FCSTD DOCUMENT  (FreeCAD 0.16R6707 (Git))
Label: temp
License: All rights reserved
LicenseURL: http://en.wikipedia.org/wiki/All_rights_reserved
objects: Sketcher::SketchObject×1
note: 1 computed .brp shape members not serialized (recipe doc carries the construction recipe); baked Part::Feature solids carry a one-line shape summary decoded from their .brp

FEATURE [Sketcher::SketchObject] Sketch006
  sketch-geometry (47):
    g0: LineSegment [constr] StartX=-190 StartY=250 StartZ=0 EndX=0 EndY=250 EndZ=0
    g1: LineSegment [constr] StartX=0 StartY=250 StartZ=0 EndX=0 EndY=0 EndZ=0
    g2: LineSegment [constr] StartX=0 StartY=0 StartZ=0 EndX=-190 EndY=0 EndZ=0
    g3: LineSegment [constr] StartX=-190 StartY=0 StartZ=0 EndX=-190 EndY=250 EndZ=0
    g4: LineSegment [constr] StartX=-152.5 StartY=78.75 StartZ=0 EndX=-37.5 EndY=78.75 EndZ=0
    g5: LineSegment [constr] StartX=-37.5 StartY=78.75 StartZ=0 EndX=-37.5 EndY=13.75 EndZ=0
    g6: LineSegment [constr] StartX=-37.5 StartY=13.75 StartZ=0 EndX=-152.5 EndY=13.75 EndZ=0
    g7: LineSegment [constr] StartX=-152.5 StartY=13.75 StartZ=0 EndX=-152.5 EndY=78.75 EndZ=0
    g8: Circle CenterX=-147.5 CenterY=68.75 CenterZ=0 NormalX=0 NormalY=0 NormalZ=1 Radius=2
    g9: Circle CenterX=-147.5 CenterY=23.75 CenterZ=0 NormalX=0 NormalY=0 NormalZ=1 Radius=2
    g10: Circle CenterX=-42.5 CenterY=68.75 CenterZ=0 NormalX=0 NormalY=0 NormalZ=1 Radius=2
    g11: Circle CenterX=-42.5 CenterY=23.75 CenterZ=0 NormalX=0 NormalY=0 NormalZ=1 Radius=2
    g12: LineSegment [constr] StartX=-152.5 StartY=78.75 StartZ=0 EndX=-147.5 EndY=68.75 EndZ=0
    g13: LineSegment [constr] StartX=-152.5 StartY=13.75 StartZ=0 EndX=-147.5 EndY=23.75 EndZ=0
    g14: LineSegment [constr] StartX=-42.5 StartY=23.75 StartZ=0 EndX=-37.5 EndY=13.75 EndZ=0
    g15: LineSegment [constr] StartX=-152.5 StartY=157.5 StartZ=0 EndX=-37.5 EndY=157.5 EndZ=0
    g16: LineSegment [constr] StartX=-37.5 StartY=157.5 StartZ=0 EndX=-37.5 EndY=92.5 EndZ=0
    g17: LineSegment [constr] StartX=-37.5 StartY=92.5 StartZ=0 EndX=-152.5 EndY=92.5 EndZ=0
    g18: LineSegment [constr] StartX=-152.5 StartY=92.5 StartZ=0 EndX=-152.5 EndY=157.5 EndZ=0
    g19: Circle CenterX=-147.5 CenterY=147.5 CenterZ=0 NormalX=0 NormalY=0 NormalZ=1 Radius=2
    g20: Circle CenterX=-147.5 CenterY=102.5 CenterZ=0 NormalX=0 NormalY=0 NormalZ=1 Radius=2
    g21: Circle CenterX=-42.5 CenterY=147.5 CenterZ=0 NormalX=0 NormalY=0 NormalZ=1 Radius=2
    g22: Circle CenterX=-42.5 CenterY=102.5 CenterZ=0 NormalX=0 NormalY=0 NormalZ=1 Radius=2
    g23: LineSegment [constr] StartX=-152.5 StartY=157.5 StartZ=0 EndX=-147.5 EndY=147.5 EndZ=0
    g24: LineSegment [constr] StartX=-152.5 StartY=92.5 StartZ=0 EndX=-147.5 EndY=102.5 EndZ=0
    g25: LineSegment [constr] StartX=-42.5 StartY=102.5 StartZ=0 EndX=-37.5 EndY=92.5 EndZ=0
    g26: LineSegment [constr] StartX=-152.5 StartY=236.25 StartZ=0 EndX=-37.5 EndY=236.25 EndZ=0
    g27: LineSegment [constr] StartX=-37.5 StartY=236.25 StartZ=0 EndX=-37.5 EndY=171.25 EndZ=0
    g28: LineSegment [constr] StartX=-37.5 StartY=171.25 StartZ=0 EndX=-152.5 EndY=171.25 EndZ=0
    g29: LineSegment [constr] StartX=-152.5 StartY=171.25 StartZ=0 EndX=-152.5 EndY=236.25 EndZ=0
    g30: Circle CenterX=-147.5 CenterY=226.25 CenterZ=0 NormalX=0 NormalY=0 NormalZ=1 Radius=2
    g31: Circle CenterX=-147.5 CenterY=181.25 CenterZ=0 NormalX=0 NormalY=0 NormalZ=1 Radius=2
    g32: Circle CenterX=-42.5 CenterY=226.25 CenterZ=0 NormalX=0 NormalY=0 NormalZ=1 Radius=2
    g33: Circle CenterX=-42.5 CenterY=181.25 CenterZ=0 NormalX=0 NormalY=0 NormalZ=1 Radius=2
    g34: LineSegment [constr] StartX=-152.5 StartY=236.25 StartZ=0 EndX=-147.5 EndY=226.25 EndZ=0
    g35: LineSegment [constr] StartX=-152.5 StartY=171.25 StartZ=0 EndX=-147.5 EndY=181.25 EndZ=0
    g36: LineSegment [constr] StartX=-42.5 StartY=181.25 StartZ=0 EndX=-37.5 EndY=171.25 EndZ=0
    g37: LineSegment [constr] StartX=-37.5 StartY=13.75 StartZ=0 EndX=-37.5 EndY=0 EndZ=0
    g38: LineSegment [constr] StartX=-37.5 StartY=78.75 StartZ=0 EndX=-37.5 EndY=92.5 EndZ=0
    g39: LineSegment [constr] StartX=-37.5 StartY=157.5 StartZ=0 EndX=-37.5 EndY=171.25 EndZ=0
    g40: LineSegment [constr] StartX=-37.5 StartY=236.25 StartZ=0 EndX=-37.5 EndY=250 EndZ=0
    g41: LineSegment [constr] StartX=-152.5 StartY=236.25 StartZ=0 EndX=-190 EndY=236.25 EndZ=0
    g42: LineSegment [constr] StartX=-37.5 StartY=236.25 StartZ=0 EndX=0 EndY=236.25 EndZ=0
    g43: LineSegment StartX=-190 StartY=250 StartZ=0 EndX=0 EndY=250 EndZ=0
    g44: LineSegment StartX=0 StartY=250 StartZ=0 EndX=0 EndY=0 EndZ=0
    g45: LineSegment StartX=0 StartY=0 StartZ=0 EndX=-190 EndY=0 EndZ=0
    g46: LineSegment StartX=-190 StartY=0 StartZ=0 EndX=-190 EndY=250 EndZ=0
  constraints (127):
    c: Coincident(g0,g1)
    c: Coincident(g1,g2)
    c: Coincident(g2,g3)
    c: Coincident(g3,g0)
    c: Horizontal(g0)
    c: Horizontal(g2)
    c: Vertical(g1)
    c: Vertical(g3)
    c: Coincident(g4,g5)
    c: Coincident(g5,g6)
    c: Coincident(g6,g7)
    c: Coincident(g7,g4)
    c: Horizontal(g4)
    c: Horizontal(g6)
    c: Vertical(g5)
    c: Vertical(g7)
    c: DistanceX(g4,g4) = 115
    c: DistanceY(g5,g5) = 65
    c: Radius(g8) = 2
    c: Equal(g8,g9)
    c: Equal(g8,g10)
    c: Equal(g8,g11)
    c: DistanceY(g9,g8) = 45
    c: DistanceY(g9,g11) = 0
    c: DistanceY(g10,g8) = 0
    c: DistanceX(g8,g10) = 105
    c: DistanceX(g11,g10) = 0
    c: DistanceX(g8,g9) = 0
    c: Coincident(g12,g4)
    c: Coincident(g12,g8)
    c: Coincident(g13,g6)
    c: Coincident(g13,g9)
    c: Coincident(g14,g11)
    c: Coincident(g14,g5)
    c: Equal(g14,g13)
    c: Equal(g13,g12)
    c: Coincident(g15,g16)
    c: Coincident(g16,g17)
    c: Coincident(g17,g18)
    c: Coincident(g18,g15)
    c: Horizontal(g15)
    c: Horizontal(g17)
    c: Vertical(g16)
    c: Vertical(g18)
    c: Equal(g4,g15) = 115
    c: Equal(g5,g16) = 65
    c: Equal(g8,g19) = 2
    c: Equal(g19,g20)
    c: Equal(g19,g21)
    c: Equal(g19,g22)
    c: DistanceY(g20,g19) = 45
    c: DistanceY(g20,g22) = 0
    c: DistanceY(g21,g19) = 0
    c: DistanceX(g19,g21) = 105
    c: DistanceX(g22,g21) = 0
    c: DistanceX(g19,g20) = 0
    c: Coincident(g23,g15)
    c: Coincident(g23,g19)
    c: Coincident(g24,g17)
    c: Coincident(g24,g20)
    c: Coincident(g25,g22)
    c: Coincident(g25,g16)
    c: Equal(g25,g24)
    c: Equal(g24,g23)
    c: Coincident(g26,g27)
    c: Coincident(g27,g28)
    c: Coincident(g28,g29)
    c: Coincident(g29,g26)
    c: Horizontal(g26)
    c: Horizontal(g28)
    c: Vertical(g27)
    c: Vertical(g29)
    c: Equal(g4,g26) = 115
    c: Equal(g5,g27) = 65
    c: Equal(g8,g30) = 2
    c: Equal(g30,g31)
    c: Equal(g30,g32)
    c: Equal(g30,g33)
    c: DistanceY(g31,g30) = 45
    c: DistanceY(g31,g33) = 0
    c: DistanceY(g32,g30) = 0
    c: DistanceX(g30,g32) = 105
    c: DistanceX(g33,g32) = 0
    c: DistanceX(g30,g31) = 0
    c: Coincident(g34,g26)
    c: Coincident(g34,g30)
    c: Coincident(g35,g28)
    c: Coincident(g35,g31)
    c: Coincident(g36,g33)
    c: Coincident(g36,g27)
    c: Equal(g36,g35)
    c: Equal(g35,g34)
    c: Coincident(g37,g5)
    c: PointOnObject(g37,g2)
    c: Vertical(g37)
    c: Coincident(g38,g4)
    c: Coincident(g38,g16)
    c: Vertical(g38)
    c: Coincident(g39,g15)
    c: Coincident(g39,g27)
    c: Vertical(g39)
    c: Coincident(g40,g26)
    c: PointOnObject(g40,g0)
    c: Vertical(g40)
    c: Equal(g40,g39)
    c: Equal(g39,g38)
    c: Equal(g38,g37)
    c: Coincident(g41,g26)
    c: PointOnObject(g41,g3)
    c: Horizontal(g41)
    c: Coincident(g42,g26)
    c: PointOnObject(g42,g1)
    c: Horizontal(g42)
    c: Equal(g42,g41)
    c: DistanceY(g3,g3) = 250
    c: DistanceX(g2,g2) = 190
    c: Coincident(g1,g-1)
    c: Coincident(g43,g44)
    c: Coincident(g44,g45)
    c: Coincident(g45,g46)
    c: Coincident(g46,g43)
    c: Horizontal(g43)
    c: Horizontal(g45)
    c: Vertical(g44)
    c: Vertical(g46)
    c: Coincident(g43,g0)
    c: Coincident(g44,g-1)
